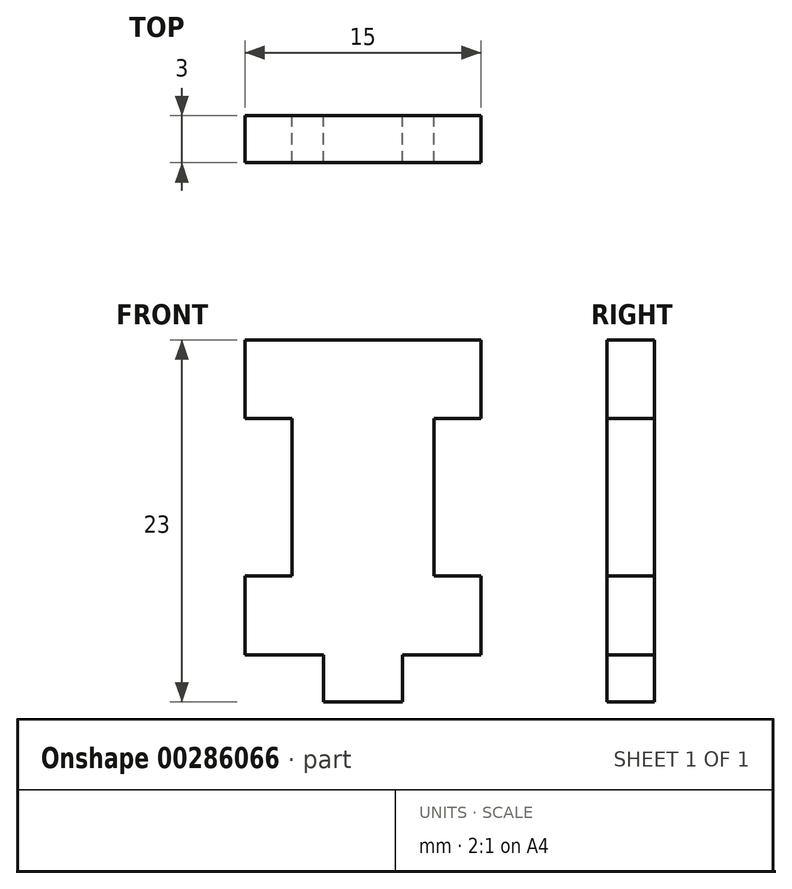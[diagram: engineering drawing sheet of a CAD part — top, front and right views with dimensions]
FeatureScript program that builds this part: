
annotation { "Feature Type Name" : "Feature", "Feature Type Description" : "" }
export const myFeature = defineFeature(function(context is Context, id is Id, definition is map)
    precondition{}
    {
        {
            var Q0;
            Q0=qCreatedBy(makeId("Front.planeOp"),FACE);
            var sketch = newSketch(context, id + "F0", { "sketchPlane" : qUnion([Q0])});
            skLineSegment(sketch, "E0", {"start": v(0, 10) * mm, "end": v(-7.5, 10) * mm});
            skLineSegment(sketch, "E1", {"start": v(-7.5, 10) * mm, "end": v(-7.5, 5) * mm});
            skLineSegment(sketch, "E2", {"start": v(-7.5, 5) * mm, "end": v(-4.5, 5) * mm});
            skLineSegment(sketch, "E3", {"start": v(-4.5, 5) * mm, "end": v(-4.5, -5) * mm});
            skLineSegment(sketch, "E4", {"start": v(-4.5, -5) * mm, "end": v(-7.5, -5) * mm});
            skLineSegment(sketch, "E5", {"start": v(-7.5, -5) * mm, "end": v(-7.5, -10) * mm});
            skLineSegment(sketch, "E6", {"start": v(-7.5, -10) * mm, "end": v(-2.5, -10) * mm});
            skLineSegment(sketch, "E7", {"start": v(-2.5, -10) * mm, "end": v(-2.5, -13) * mm});
            skLineSegment(sketch, "E8", {"start": v(-2.5, -13) * mm, "end": v(0, -13) * mm});
            skLineSegment(sketch, "E9.MirrorCS", {"start": v(0, 10) * mm, "end": v(7.5, 10) * mm});
            skLineSegment(sketch, "E10.MirrorCS", {"start": v(7.5, 10) * mm, "end": v(7.5, 5) * mm});
            skLineSegment(sketch, "E11.MirrorCS", {"start": v(7.5, -5) * mm, "end": v(7.5, -10) * mm});
            skLineSegment(sketch, "E12.MirrorCS", {"start": v(4.5, 5) * mm, "end": v(4.5, -5) * mm});
            skLineSegment(sketch, "E13.MirrorCS", {"start": v(7.5, -10) * mm, "end": v(2.5, -10) * mm});
            skLineSegment(sketch, "E14.MirrorCS", {"start": v(4.5, -5) * mm, "end": v(7.5, -5) * mm});
            skLineSegment(sketch, "E15.MirrorCS", {"start": v(2.5, -10) * mm, "end": v(2.5, -13) * mm});
            skLineSegment(sketch, "E16.MirrorCS", {"start": v(7.5, 5) * mm, "end": v(4.5, 5) * mm});
            skLineSegment(sketch, "E17.MirrorCS", {"start": v(2.5, -13) * mm, "end": v(0, -13) * mm});
            skSolve(sketch);
        }
        {
            var Q0;
            Q0=makeQuery(id+"F0.imprint","IMPRINT",FACE,{"disambiguationData":[TD([[makeQuery(id+"F0.imprint","IMPRINT",EDGE,{"derivedFrom":sQuery(id+"F0.wireOp",EDGE,"E0")}),1.0]])]});
            extrude(context, id + "F1", {"entities" : qUnion([Q0]), "depth" : 3 * mm});
        }
    });
